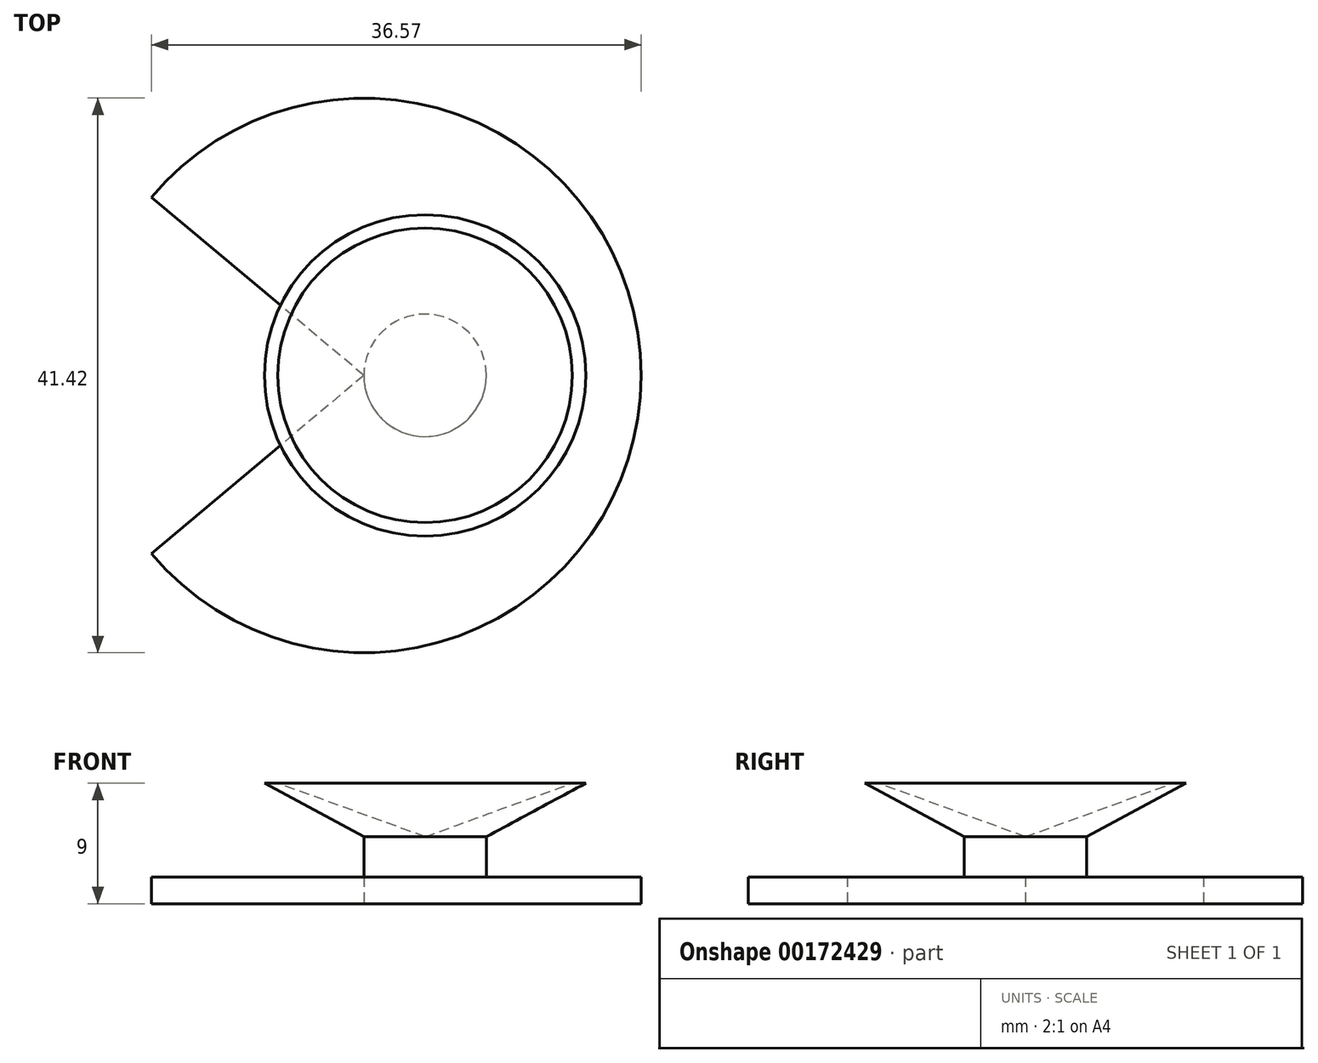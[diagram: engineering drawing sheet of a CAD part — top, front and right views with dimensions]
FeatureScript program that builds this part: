
annotation { "Feature Type Name" : "Feature", "Feature Type Description" : "" }
export const myFeature = defineFeature(function(context is Context, id is Id, definition is map)
    precondition{}
    {
        {
            var Q0;
            Q0=qCreatedBy(makeId("Top.planeOp"),FACE);
            var sketch = newSketch(context, id + "F0", { "sketchPlane" : qUnion([Q0])});
            skCircle(sketch, "E0", {"center": v(0, 0) * mm, "radius": 20.7 * mm});
            skLineSegment(sketch, "E1", {"start": v(0, 0) * mm, "end": v(-15.86, 13.31) * mm});
            skLineSegment(sketch, "E2", {"start": v(0, 0) * mm, "end": v(-15.86, -13.31) * mm});
            skLineSegment(sketch, "E3", {"start": v(0, 0) * mm, "end": v(-20.7, 0) * mm, "construction": true});
            skSolve(sketch);
        }
        {
            var Q0;
            {var subQ0=sQuery(id+"F0.wireOp",EDGE,"E1");Q0=makeQuery(id+"F0.imprint","IMPRINT",FACE,{"disambiguationData":[TD([[makeQuery(id+"F0.imprint","IMPRINT",EDGE,{"derivedFrom":subQ0}),-1.0]])]});}
            extrude(context, id + "F1", {"entities" : qUnion([Q0]), "depth" : 2 * mm});
        }
        {
            var Q0;
            Q0=makeQuery(id+"F1.opExtrude","CAP_FACE",FACE,{"disambiguationData":[OSD([sQuery(id+"F0.wireOp",EDGE,"E0"),sQuery(id+"F0.wireOp",EDGE,"E1"),sQuery(id+"F0.wireOp",EDGE,"E2")])],"isStart":false});
            var sketch = newSketch(context, id + "F2", { "sketchPlane" : qUnion([Q0])});
            skCircle(sketch, "E4", {"center": v(4.58, 0) * mm, "radius": 4.58 * mm});
            skSolve(sketch);
        }
        {
            var Q0;
            Q0=qSketchRegion(id+"F2",true);
            extrude(context, id + "F3", {"entities" : qUnion([Q0]), "operationType" : NewBodyOperationType.ADD, "depth" : 3 * mm});
        }
        {
            var Q0;
            Q0=makeQuery(id+"F3.opExtrude","CAP_FACE",FACE,{"disambiguationData":[OSD([sQuery(id+"F2.wireOp",EDGE,"E4")])],"isStart":false});
            cPlane(context, id + "F4", {"entities" : qUnion([Q0]), "cplaneType" : CPlaneType.OFFSET, "offset" : 4 * mm, "width" : 150 * mm, "height" : 150 * mm});
        }
        {
            var Q0;
            Q0=qCreatedBy(id+"F4.planeOp",FACE);
            var sketch = newSketch(context, id + "F5", { "sketchPlane" : qUnion([Q0])});
            skCircle(sketch, "E5.0", {"center": v(4.58, 0) * mm, "radius": 4.58 * mm, "construction": true});
            skCircle(sketch, "E6", {"center": v(4.58, 0) * mm, "radius": 12 * mm});
            skSolve(sketch);
        }
        {
            var Q0;
            Q0=makeQuery(id+"F3.opExtrude","CAP_FACE",FACE,{"disambiguationData":[OSD([sQuery(id+"F2.wireOp",EDGE,"E4")])],"isStart":false});
            var sketch = newSketch(context, id + "F6", { "sketchPlane" : qUnion([Q0])});
            skPoint(sketch, "E7", {"position": v(4.58, 0) * mm});
            skSolve(sketch);
        }
        {
            var Q1;
            Q1=makeQuery(id+"F5.imprint","IMPRINT",FACE,{"disambiguationData":[TD([[makeQuery(id+"F5.imprint","IMPRINT",EDGE,{"derivedFrom":sQuery(id+"F5.wireOp",EDGE,"E6")}),1.0]])]});
            var Q2;
            Q2=makeQuery(id+"F3.opExtrude","CAP_FACE",FACE,{"disambiguationData":[OSD([sQuery(id+"F2.wireOp",EDGE,"E4")])],"isStart":false});
            loft(context, id + "F7", {"operationType" : NewBodyOperationType.ADD, "sheetProfilesArray" : [{ "sheetProfileEntities" : qUnion([Q1]) }, { "sheetProfileEntities" : qUnion([Q2]) }]});
        }
        {
            var Q0;
            Q0=makeQuery(id+"F7.opLoft","CAP_FACE",FACE,{"disambiguationData":[OSD([makeQuery(id+"F5.imprint","IMPRINT",FACE,{"disambiguationData":[TD([[makeQuery(id+"F5.imprint","IMPRINT",EDGE,{"derivedFrom":sQuery(id+"F5.wireOp",EDGE,"E6")}),1.0]])]})])],"isStart":true});
            var sketch = newSketch(context, id + "F8", { "sketchPlane" : qUnion([Q0])});
            skCircle(sketch, "E8", {"center": v(4.58, 0) * mm, "radius": 11 * mm});
            skLineSegment(sketch, "E9", {"start": v(4.58, 11) * mm, "end": v(4.58, 12) * mm, "construction": true});
            skSolve(sketch);
        }
        {
            var Q1;
            Q1=makeQuery(id+"F8.imprint","IMPRINT",FACE,{"disambiguationData":[TD([[makeQuery(id+"F8.imprint","IMPRINT",EDGE,{"derivedFrom":sQuery(id+"F8.wireOp",EDGE,"E8")}),1.0]])]});
            var Q2;
            Q2=sQuery(id+"F6.wireOp",VERTEX,"E7");
            loft(context, id + "F9", {"operationType" : NewBodyOperationType.REMOVE, "sheetProfilesArray" : [{ "sheetProfileEntities" : qUnion([Q1]) }, { "sheetProfileEntities" : qUnion([Q2]) }]});
        }
    });
